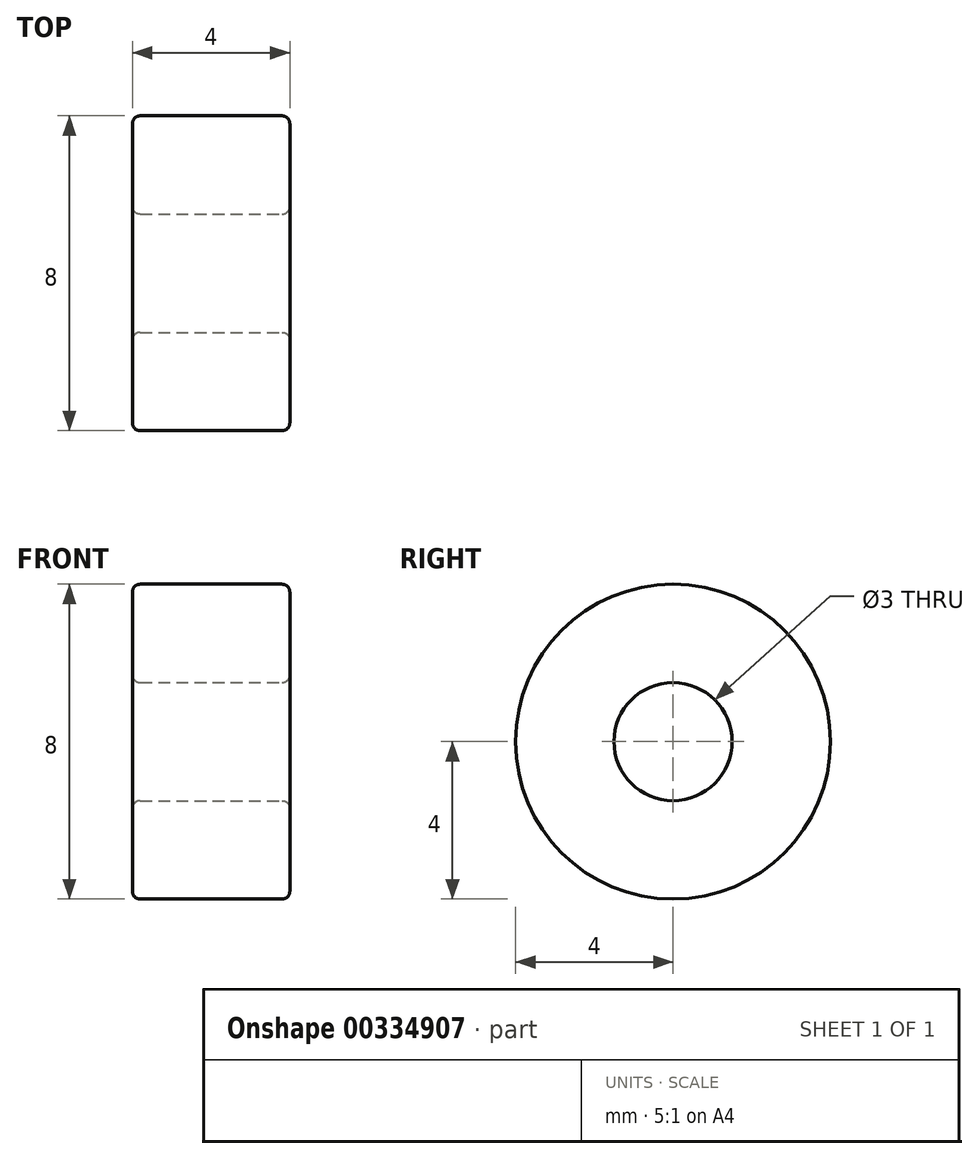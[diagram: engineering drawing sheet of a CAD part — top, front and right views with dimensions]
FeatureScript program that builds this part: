
annotation { "Feature Type Name" : "Feature", "Feature Type Description" : "" }
export const myFeature = defineFeature(function(context is Context, id is Id, definition is map)
    precondition{}
    {
        {
            var Q0;
            Q0=qCreatedBy(makeId("Front.planeOp"),FACE);
            var sketch = newSketch(context, id + "F0", { "sketchPlane" : qUnion([Q0])});
            skLineSegment(sketch, "E0.bottom", {"start": v(-2, 4) * mm, "end": v(2, 4) * mm});
            skLineSegment(sketch, "E0.top", {"start": v(-2, 1.5) * mm, "end": v(2, 1.5) * mm});
            skLineSegment(sketch, "E0.left", {"start": v(-2, 4) * mm, "end": v(-2, 1.5) * mm});
            skLineSegment(sketch, "E0.right", {"start": v(2, 4) * mm, "end": v(2, 1.5) * mm});
            skPoint(sketch, "E1", {"position": v(0, 4) * mm});
            skLineSegment(sketch, "E2", {"start": v(3.48, 0) * mm, "end": v(-3.72, 0) * mm, "construction": true});
            skSolve(sketch);
        }
        {
            var Q0;
            Q0 = qSketchRegion(id + "F0", true);
            var Q1;
            Q1=sQuery(id+"F0.wireOp",EDGE,"E2");
            revolve(context, id + "F1", {"entities" : qUnion([Q0]), "axis" : qUnion([Q1]), "revolveType" : RevolveType.FULL});
        }
        {
            var Q0;
            Q0=makeQuery(id+"F1.opRevolve","SWEPT_EDGE",EDGE,{"disambiguationData":[OSD([sQuery(id+"F0.wireOp",EDGE,"E0.bottom"),sQuery(id+"F0.wireOp",EDGE,"E0.left")])]});
            var Q1;
            Q1=makeQuery(id+"F1.opRevolve","SWEPT_EDGE",EDGE,{"disambiguationData":[OSD([sQuery(id+"F0.wireOp",EDGE,"E0.top"),sQuery(id+"F0.wireOp",EDGE,"E0.left")])]});
            var Q2;
            Q2=makeQuery(id+"F1.opRevolve","SWEPT_EDGE",EDGE,{"disambiguationData":[OSD([sQuery(id+"F0.wireOp",EDGE,"E0.bottom"),sQuery(id+"F0.wireOp",EDGE,"E0.right")])]});
            var Q3;
            Q3=makeQuery(id+"F1.opRevolve","SWEPT_EDGE",EDGE,{"disambiguationData":[OSD([sQuery(id+"F0.wireOp",EDGE,"E0.top"),sQuery(id+"F0.wireOp",EDGE,"E0.right")])]});
            fillet(context, id + "F2", {"entities" : qUnion([Q0, Q1, Q2, Q3]), "radius" : 0.2 * mm, "tangentPropagation" : true, "allowEdgeOverflow" : false});
        }
    });
